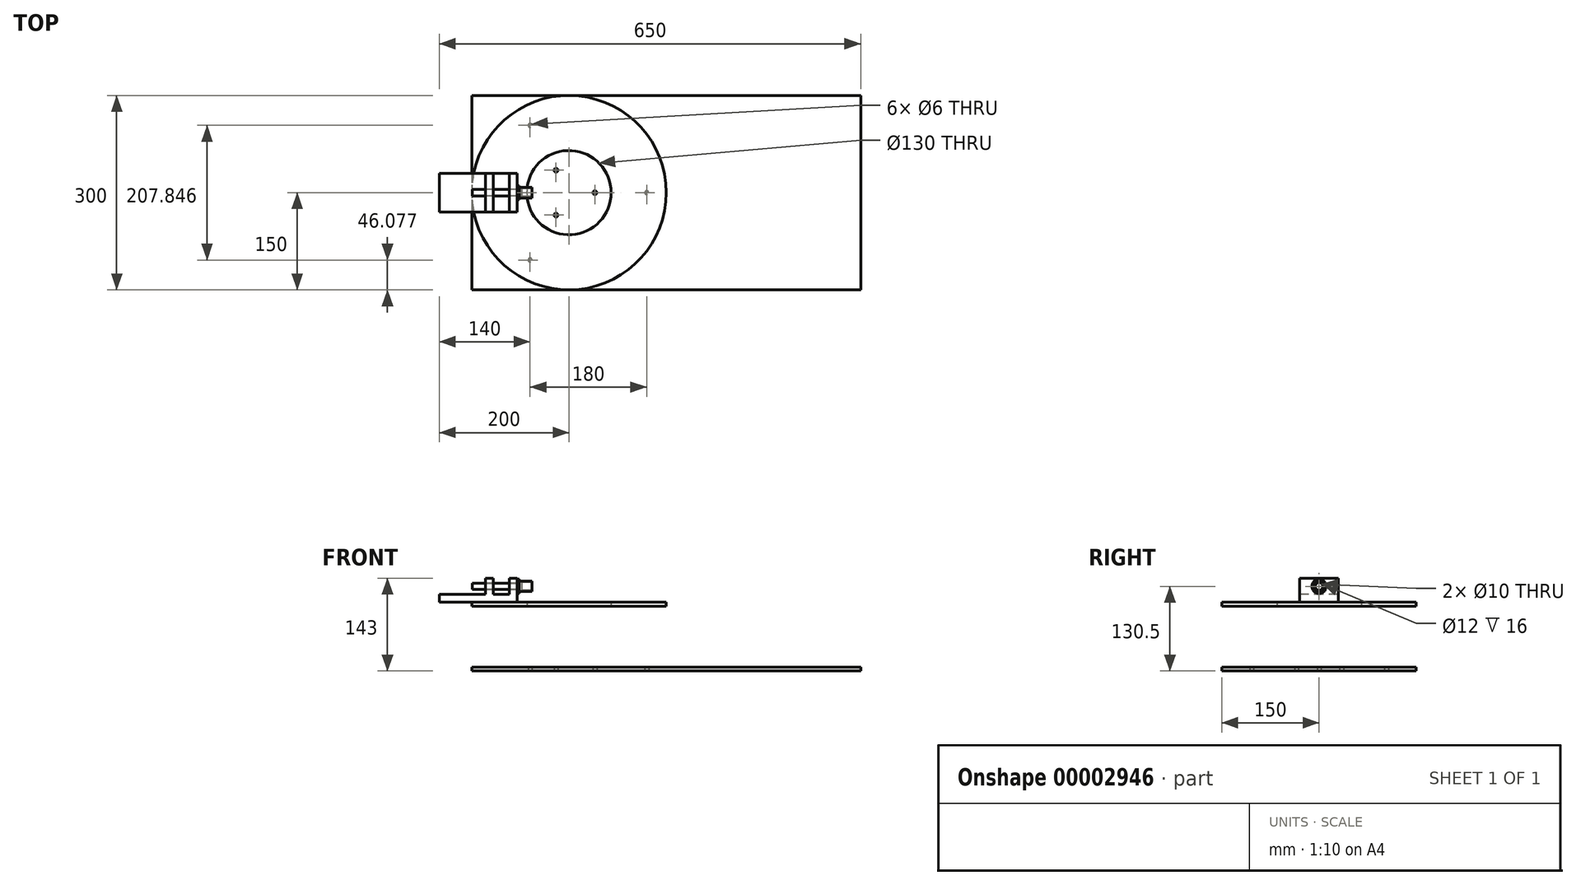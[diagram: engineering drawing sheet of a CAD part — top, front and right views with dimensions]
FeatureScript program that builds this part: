
annotation { "Feature Type Name" : "Feature", "Feature Type Description" : "" }
export const myFeature = defineFeature(function(context is Context, id is Id, definition is map)
    precondition{}
    {
        {
            var Q0;
            Q0=qCreatedBy(makeId("Top.planeOp"),FACE);
            var sketch = newSketch(context, id + "F0", { "sketchPlane" : qUnion([Q0])});
            skLineSegment(sketch, "E0", {"start": v(0, 0) * mm, "end": v(-60, 103.92) * mm, "construction": true});
            skLineSegment(sketch, "E1", {"start": v(0, 0) * mm, "end": v(120, 0) * mm, "construction": true});
            skLineSegment(sketch, "E2", {"start": v(0, 0) * mm, "end": v(-60, -103.92) * mm, "construction": true});
            skCircle(sketch, "E3", {"center": v(0, 0) * mm, "radius": 120 * mm, "construction": true});
            skCircle(sketch, "E4", {"center": v(0, 0) * mm, "radius": 40 * mm, "construction": true});
            skCircle(sketch, "E5", {"center": v(-60, 103.92) * mm, "radius": 3 * mm});
            skCircle(sketch, "E6", {"center": v(-20, 34.64) * mm, "radius": 3 * mm});
            skCircle(sketch, "E7", {"center": v(40, 0) * mm, "radius": 3 * mm});
            skCircle(sketch, "E8", {"center": v(120, 0) * mm, "radius": 3 * mm});
            skCircle(sketch, "E9", {"center": v(-20, -34.64) * mm, "radius": 3 * mm});
            skCircle(sketch, "E10", {"center": v(-60, -103.92) * mm, "radius": 3 * mm});
            skLineSegment(sketch, "E11.bottom", {"start": v(-150, 150) * mm, "end": v(450, 150) * mm});
            skLineSegment(sketch, "E11.top", {"start": v(-150, -150) * mm, "end": v(450, -150) * mm});
            skLineSegment(sketch, "E11.left", {"start": v(-150, 150) * mm, "end": v(-150, -150) * mm});
            skLineSegment(sketch, "E11.right", {"start": v(450, 150) * mm, "end": v(450, -150) * mm});
            skSolve(sketch);
        }
        {
            var Q0;
            Q0=makeQuery(id+"F0.imprint","IMPRINT",FACE,{"disambiguationData":[TD([[makeQuery(id+"F0.imprint","IMPRINT",EDGE,{"derivedFrom":sQuery(id+"F0.wireOp",EDGE,"53a08d33-a2c4-403e-a201-b9b804abc25b")}),1.0]])]});
            var Q1;
            Q1=makeQuery(id+"F0.imprint","IMPRINT",FACE,{"disambiguationData":[TD([[makeQuery(id+"F0.imprint","IMPRINT",EDGE,{"derivedFrom":sQuery(id+"F0.wireOp",EDGE,"E5")}),-1.0]])]});
            extrude(context, id + "F1", {"entities" : qUnion([Q0, Q1]), "depth" : 6 * mm});
        }
        {
            var Q0;
            Q0=qCreatedBy(makeId("Top.planeOp"),FACE);
            cPlane(context, id + "F2", {"entities" : qUnion([Q0]), "cplaneType" : CPlaneType.OFFSET, "offset" : 100 * mm, "width" : 150 * mm, "height" : 150 * mm});
        }
        {
            var Q0;
            Q0=qCreatedBy(id+"F2.planeOp",FACE);
            var sketch = newSketch(context, id + "F3", { "sketchPlane" : qUnion([Q0])});
            skCircle(sketch, "E12", {"center": v(0, 0) * mm, "radius": 150 * mm});
            skCircle(sketch, "E13", {"center": v(0, 0) * mm, "radius": 65 * mm});
            skSolve(sketch);
        }
        {
            var Q0;
            Q0=makeQuery(id+"F3.imprint","IMPRINT",FACE,{"disambiguationData":[TD([[makeQuery(id+"F3.imprint","IMPRINT",EDGE,{"derivedFrom":sQuery(id+"F3.wireOp",EDGE,"E12")}),1.0]])]});
            extrude(context, id + "F4", {"entities" : qUnion([Q0]), "depth" : 6 * mm});
        }
        {
            var Q0;
            Q0=makeQuery(id+"F4.opExtrude","CAP_FACE",FACE,{"disambiguationData":[OSD([sQuery(id+"F3.wireOp",EDGE,"E12"),sQuery(id+"F3.wireOp",EDGE,"E13")])],"isStart":false});
            var sketch = newSketch(context, id + "F5", { "sketchPlane" : qUnion([Q0])});
            skLineSegment(sketch, "E14.bottom", {"start": v(-200, 30) * mm, "end": v(-80, 30) * mm});
            skLineSegment(sketch, "E14.top", {"start": v(-200, -30) * mm, "end": v(-80, -30) * mm});
            skLineSegment(sketch, "E14.left", {"start": v(-200, 30) * mm, "end": v(-200, -30) * mm});
            skLineSegment(sketch, "E14.right", {"start": v(-80, 30) * mm, "end": v(-80, -30) * mm});
            skLineSegment(sketch, "E15", {"start": v(0, 0) * mm, "end": v(-200, 0) * mm, "construction": true});
            skSolve(sketch);
        }
        {
            var Q0;
            {var subQ5=sQuery(id+"F5.wireOp",EDGE,"E14.left");Q0=makeQuery(id+"F5.imprint","IMPRINT",FACE,{"disambiguationData":[TD([[makeQuery(id+"F5.imprint","IMPRINT",EDGE,{"derivedFrom":subQ5}),1.0]])]});}
            var Q1;
            {var subQ3=sQuery(id+"F5.wireOp",EDGE,"E14.bottom");var subQ5=sQuery(id+"F5.wireOp",EDGE,"E14.right");var subQ6=makeQuery(id+"F5.imprint","INTERSECT",VERTEX,{"derivedFrom":[subQ3,subQ5]});Q1=makeQuery(id+"F5.imprint","IMPRINT",FACE,{"disambiguationData":[TD([[makeQuery(id+"F5.imprint","IMPRINT",EDGE,{"disambiguationData":[TD([[subQ6,1.0]])],"derivedFrom":subQ3}),-1.0]])]});}
            var Q2;
            {var subQ5=sQuery(id+"F5.wireOp",EDGE,"586a50a9-9a21-45ab-90f8-c84c7e54c170");Q2=makeQuery(id+"F5.imprint","IMPRINT",FACE,{"disambiguationData":[TD([[makeQuery(id+"F5.imprint","IMPRINT",EDGE,{"derivedFrom":subQ5}),-1.0]])]});}
            extrude(context, id + "F6", {"entities" : qUnion([Q0, Q1, Q2]), "depth" : 12 * mm});
        }
        {
            var Q0;
            Q0=makeQuery(id+"F6.opExtrude","CAP_FACE",FACE,{"disambiguationData":[OSD([sQuery(id+"F5.wireOp",EDGE,"E14.bottom"),sQuery(id+"F5.wireOp",EDGE,"E14.top"),sQuery(id+"F5.wireOp",EDGE,"E14.left"),sQuery(id+"F5.wireOp",EDGE,"E14.right")])],"isStart":false});
            var sketch = newSketch(context, id + "F7", { "sketchPlane" : qUnion([Q0])});
            skLineSegment(sketch, "E16.bottom", {"start": v(-80, 30) * mm, "end": v(-92, 30) * mm});
            skLineSegment(sketch, "E16.top", {"start": v(-80, -30) * mm, "end": v(-92, -30) * mm});
            skLineSegment(sketch, "E16.left", {"start": v(-80, 30) * mm, "end": v(-80, -30) * mm});
            skLineSegment(sketch, "E16.right", {"start": v(-92, 30) * mm, "end": v(-92, -30) * mm});
            skLineSegment(sketch, "E17.bottom", {"start": v(-117, 30) * mm, "end": v(-129, 30) * mm});
            skLineSegment(sketch, "E17.top", {"start": v(-117, -30) * mm, "end": v(-129, -30) * mm});
            skLineSegment(sketch, "E17.left", {"start": v(-117, 30) * mm, "end": v(-117, -30) * mm});
            skLineSegment(sketch, "E17.right", {"start": v(-129, 30) * mm, "end": v(-129, -30) * mm});
            skSolve(sketch);
        }
        {
            var Q0;
            Q0=makeQuery(id+"F7.imprint","IMPRINT",FACE,{"disambiguationData":[TD([[makeQuery(id+"F7.imprint","IMPRINT",EDGE,{"derivedFrom":sQuery(id+"F7.wireOp",EDGE,"E17.bottom")}),-1.0]])]});
            var Q1;
            Q1=makeQuery(id+"F7.imprint","IMPRINT",FACE,{"disambiguationData":[TD([[makeQuery(id+"F7.imprint","IMPRINT",EDGE,{"derivedFrom":sQuery(id+"F7.wireOp",EDGE,"E16.bottom")}),-1.0]])]});
            extrude(context, id + "F8", {"entities" : qUnion([Q0, Q1]), "operationType" : NewBodyOperationType.ADD, "depth" : 25 * mm});
        }
        {
            var Q0;
            Q0=makeQuery(id+"F8.boolean.opBoolean","MERGE",FACE,{"derivedFrom":[makeQuery(id+"F6.opExtrude","SWEPT_FACE",FACE,{"disambiguationData":[OSD([sQuery(id+"F5.wireOp",EDGE,"E14.right")])]}),makeQuery(id+"F8.opExtrude","SWEPT_FACE",FACE,{"disambiguationData":[OSD([sQuery(id+"F7.wireOp",EDGE,"E16.left")])]})]});
            var sketch = newSketch(context, id + "F9", { "sketchPlane" : qUnion([Q0])});
            skCircle(sketch, "E18", {"center": v(0, 130.5) * mm, "radius": 5 * mm});
            skSolve(sketch);
        }
        {
            var Q0;
            Q0=makeQuery(id+"F9.imprint","IMPRINT",FACE,{"disambiguationData":[TD([[makeQuery(id+"F9.imprint","IMPRINT",EDGE,{"derivedFrom":sQuery(id+"F9.wireOp",EDGE,"E18")}),1.0]])]});
            extrude(context, id + "F10", {"entities" : qUnion([Q0]), "operationType" : NewBodyOperationType.REMOVE, "endBound" : BoundingType.THROUGH_ALL, "oppositeDirection" : true, "depth" : 25 * mm});
        }
        {
            var Q0;
            Q0=qCreatedBy(makeId("Front.planeOp"),FACE);
            var sketch = newSketch(context, id + "F11", { "sketchPlane" : qUnion([Q0])});
            skLineSegment(sketch, "E19.0", {"start": v(-129, 135.5) * mm, "end": v(-129, 125.5) * mm, "construction": true});
            skLineSegment(sketch, "E19.1", {"start": v(-80, 135.5) * mm, "end": v(-80, 125.5) * mm, "construction": true});
            skLineSegment(sketch, "E20", {"start": v(-149, 130.5) * mm, "end": v(-149, 135.5) * mm});
            skPoint(sketch, "E20.startSnap0", {"position": v(-129, 130.5) * mm});
            skLineSegment(sketch, "E21", {"start": v(-149, 135.5) * mm, "end": v(-80, 135.5) * mm});
            skLineSegment(sketch, "E22", {"start": v(-80, 141.5) * mm, "end": v(-80, 135.5) * mm});
            skLineSegment(sketch, "E23", {"start": v(-80, 141.5) * mm, "end": v(-77, 141.5) * mm});
            skLineSegment(sketch, "E24", {"start": v(-77, 141.5) * mm, "end": v(-77, 138.5) * mm});
            skPoint(sketch, "E24.endSnap0", {"position": v(-80, 130.5) * mm});
            skLineSegment(sketch, "E25", {"start": v(-77, 138.5) * mm, "end": v(-57, 138.5) * mm});
            skLineSegment(sketch, "E26", {"start": v(-57, 138.5) * mm, "end": v(-57, 130.5) * mm});
            skLineSegment(sketch, "E27", {"start": v(-149, 130.5) * mm, "end": v(-57, 130.5) * mm});
            skLineSegment(sketch, "E28", {"start": v(-73, 130.5) * mm, "end": v(-73, 136.5) * mm});
            skLineSegment(sketch, "E29", {"start": v(-73, 136.5) * mm, "end": v(-57, 136.5) * mm});
            skSolve(sketch);
        }
        {
            var Q0;
            Q0=makeQuery(id+"F11.imprint","IMPRINT",FACE,{"disambiguationData":[TD([[makeQuery(id+"F11.imprint","IMPRINT",EDGE,{"derivedFrom":sQuery(id+"F11.wireOp",EDGE,"E20")}),-1.0]])]});
            var Q1;
            Q1=sQuery(id+"F11.wireOp",EDGE,"E27");
            revolve(context, id + "F12", {"entities" : qUnion([Q0]), "axis" : qUnion([Q1]), "revolveType" : RevolveType.FULL});
        }
    });
